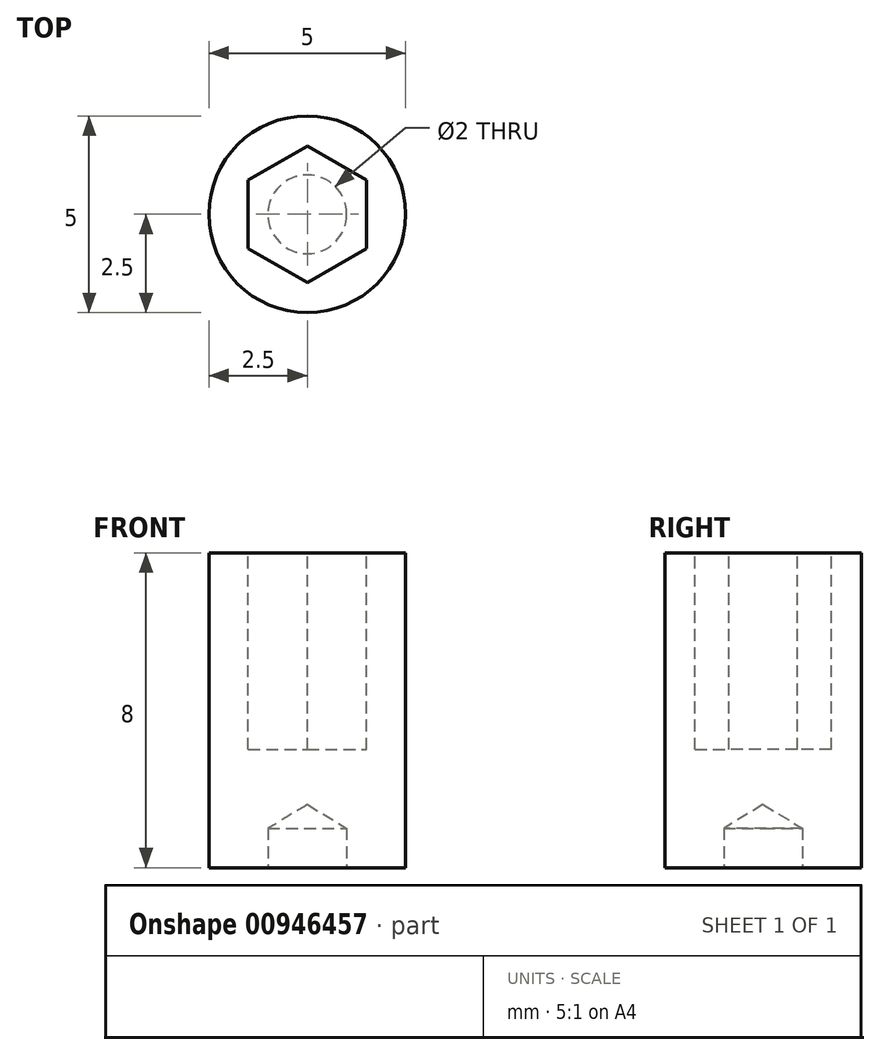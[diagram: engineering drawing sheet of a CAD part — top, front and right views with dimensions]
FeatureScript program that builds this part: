
annotation { "Feature Type Name" : "Feature", "Feature Type Description" : "" }
export const myFeature = defineFeature(function(context is Context, id is Id, definition is map)
    precondition{}
    {
        {
            var Q0;
            Q0=qCreatedBy(makeId("Top.planeOp"),FACE);
            var sketch = newSketch(context, id + "F0", { "sketchPlane" : qUnion([Q0])});
            skCircle(sketch, "E0", {"center": v(0, 0) * mm, "radius": 2.5 * mm});
            skSolve(sketch);
        }
        {
            var Q0;
            Q0=qSketchRegion(id+"F0",true);
            extrude(context, id + "F1", {"entities" : qUnion([Q0]), "depth" : 8 * mm, "offsetDistance" : 25 * mm});
        }
        {
            var Q0;
            Q0=makeQuery(id+"F1.opExtrude","CAP_FACE",FACE,{"disambiguationData":[OSD([sQuery(id+"F0.wireOp",EDGE,"E0")])],"isStart":false});
            var sketch = newSketch(context, id + "F2", { "sketchPlane" : qUnion([Q0])});
            skCircle(sketch, "E1.cCircle", {"center": v(0, 0) * mm, "radius": 1.5 * mm, "construction": true});
            skLineSegment(sketch, "E1.0", {"start": v(1.5, 0.87) * mm, "end": v(1.5, -0.87) * mm});
            skLineSegment(sketch, "E1.1", {"start": v(1.5, -0.87) * mm, "end": v(0, -1.73) * mm});
            skLineSegment(sketch, "E1.2", {"start": v(0, -1.73) * mm, "end": v(-1.5, -0.87) * mm});
            skLineSegment(sketch, "E1.3", {"start": v(-1.5, -0.87) * mm, "end": v(-1.5, 0.87) * mm});
            skLineSegment(sketch, "E1.4", {"start": v(-1.5, 0.87) * mm, "end": v(0, 1.73) * mm});
            skLineSegment(sketch, "E1.5", {"start": v(0, 1.73) * mm, "end": v(1.5, 0.87) * mm});
            skPoint(sketch, "E1.0.midPoint", {"position": v(1.5, 0) * mm});
            skSolve(sketch);
        }
        {
            var Q0;
            Q0=qSketchRegion(id+"F2",true);
            extrude(context, id + "F3", {"entities" : qUnion([Q0]), "operationType" : NewBodyOperationType.REMOVE, "oppositeDirection" : true, "depth" : 5 * mm, "offsetDistance" : 25 * mm});
        }
        {
            var Q0;
            Q0=makeQuery(id+"F1.opExtrude","CAP_FACE",FACE,{"disambiguationData":[OSD([sQuery(id+"F0.wireOp",EDGE,"E0")])],"isStart":true});
            var sketch = newSketch(context, id + "F4", { "sketchPlane" : qUnion([Q0])});
            skCircle(sketch, "E2", {"center": v(0, 0) * mm, "radius": 1 * mm});
            skSolve(sketch);
        }
        {
            var Q0;
            Q0=sQuery(id+"F4.wireOp",VERTEX,"E2.center");
            var Q1;
            Q1=makeQuery(id+"F1.opExtrude","SWEPT_BODY",BODY,{"disambiguationData":[OSD([sQuery(id+"F0.wireOp",EDGE,"E0")])]});
            hole(context, id + "F5", {"style" : HoleStyle.SIMPLE, "endStyle" : HoleEndStyle.BLIND, "holeDiameter" : 2 * mm, "majorDiameter" : 5 * mm, "holeDepth" : 1 * mm, "isTappedThrough" : true, "tappedDepth" : 12 * mm, "tapClearance" : 3, "locations" : qUnion([Q0]), "scope" : qUnion([Q1])});
        }
    });
